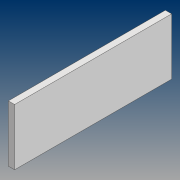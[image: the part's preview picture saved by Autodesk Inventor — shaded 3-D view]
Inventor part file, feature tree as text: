
AUTODESK INVENTOR PART (.ipt)
format: ipt  version: 2021 (Build 250183000, 183)  size: 78,336 bytes
history: native  units: mm
features: extrude x1, sketch x1
ambient origin geometry x8: Origin, YZ Plane, XZ Plane, XY Plane, X Axis, Y Axis, Z Axis, Center Point
bodies: Solid1 (feature_tree)
feature tree (2):
  extrude  "Extrusion1"  Depth=90.0mm
  sketch  "Sketch1"  dims[d0=250.0mm d1=90.0mm d2=10.0mm d3=0.0mm]
